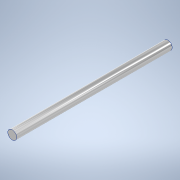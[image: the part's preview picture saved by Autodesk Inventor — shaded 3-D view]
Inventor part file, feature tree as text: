
AUTODESK INVENTOR PART (.ipt)
format: ipt  version: 2020.3 (Build 243373000, 373)  size: 95,744 bytes
history: native  units: mm
features: other x1, extrude x1, sketch x1
ambient origin geometry x8: Origin, YZ Plane, XZ Plane, XY Plane, X Axis, Y Axis, Z Axis, Center Point
bodies: Body1 (feature_tree)
feature tree (3):
  other  "ソリッド1"
  extrude  "押し出し1"  Depth=4.0mm
  sketch  "スケッチ1"
